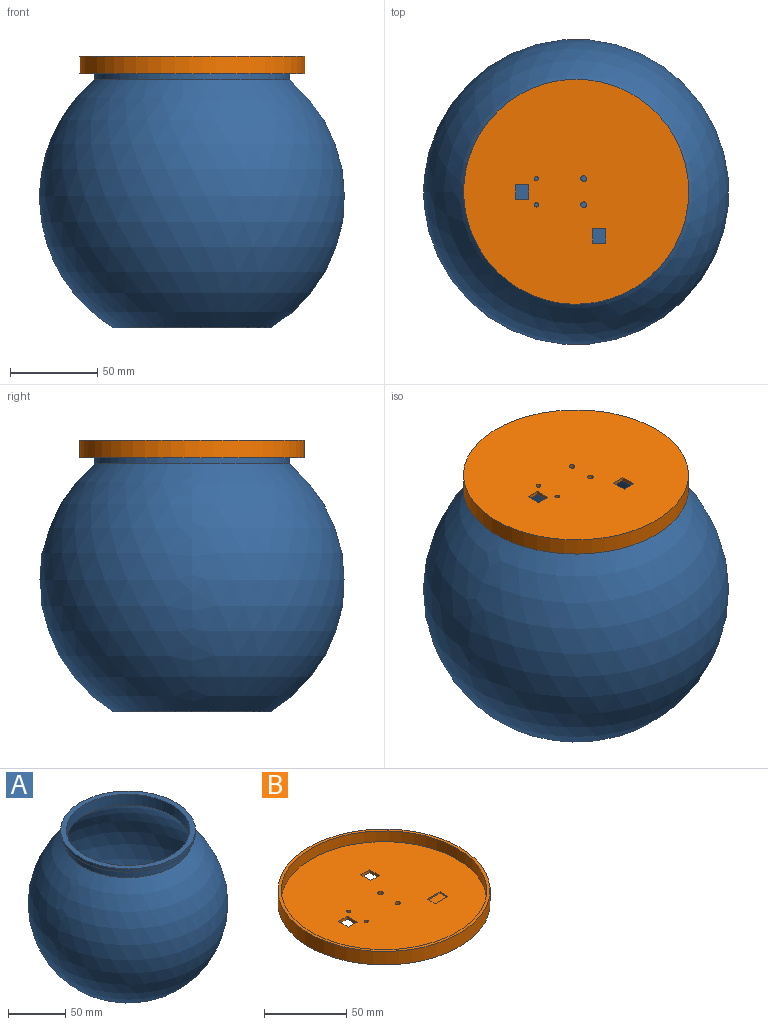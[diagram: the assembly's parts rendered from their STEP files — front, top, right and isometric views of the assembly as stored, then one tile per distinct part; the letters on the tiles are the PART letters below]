
ASSEMBLY  parts=2 mates=1
PART A: 9 faces, bbox 175x175x153.8 mm
  f0: plane 118x118mm, normal (0,0,1), area 1775mm2, adj f1,f8
  f1: cylinder r=59mm len=118mm, axis (0,0,-1), area 1297.5mm2, adj f0,f2
  f2: plane 118x118mm, normal (0,0,-1), area 1083.8mm2, adj f1,f3
  f3: cylinder r=56mm len=112mm, axis (0,0,-1), area 2814.9mm2, adj f2,f4
  f4: sphere r=87.5mm, area 78219.5mm2, adj f3,f5
  f5: plane 90x90mm, normal (0,0,-1), area 6361.7mm2, adj f4
  f6: plane 92.23x92.23mm, normal (0,0,1), area 6680.6mm2, adj f7
  f7: sphere r=86.23mm, area 75909.8mm2, adj f6,f8
  f8: cylinder r=54mm len=108mm, axis (0,0,-1), area 3901.9mm2, adj f0,f7
PART B: 22 faces, bbox 129x129x10 mm
  f0: plane 7.5x2mm, normal (0,1,0), area 15mm2, adj f1,f9,f17,f18
  f1: plane 8.5x2mm, normal (1,0,0), area 17mm2, adj f0,f2,f17,f18
  f2: plane 7.5x2mm, normal (0,-1,0), area 15mm2, adj f1,f9,f17,f18
  f3: plane 7.5x2mm, normal (0,1,0), area 15mm2, adj f4,f10,f17,f18
  f4: plane 8.5x2mm, normal (1,0,0), area 17mm2, adj f3,f5,f17,f18
  f5: plane 7.5x2mm, normal (0,-1,0), area 15mm2, adj f4,f10,f17,f18
  f6: plane 10.77x1mm, normal (0,1,0), area 10.8mm2, adj f7,f11,f17,f21
  f7: plane 6.72x1mm, normal (1,0,0), area 6.7mm2, adj f6,f8,f17,f21
  f8: plane 10.77x1mm, normal (0,-1,0), area 10.8mm2, adj f7,f11,f17,f21
  f9: plane 8.5x2mm, normal (-1,0,0), area 17mm2, adj f0,f2,f17,f18
  f10: plane 8.5x2mm, normal (-1,0,0), area 17mm2, adj f3,f5,f17,f18
  f11: plane 6.72x1mm, normal (-1,0,0), area 6.7mm2, adj f6,f8,f17,f21
  f12: cylinder r=1.25mm len=2.5mm, axis (0,0,-1), area 15.7mm2, adj f17,f18
  f13: cylinder r=1.25mm len=2.5mm, axis (0,0,-1), area 15.7mm2, adj f17,f18
  f14: cylinder r=1.65mm len=3.3mm, axis (0,0,-1), area 20.7mm2, adj f17,f18
  f15: cylinder r=1.65mm len=3.3mm, axis (0,0,-1), area 20.7mm2, adj f17,f18
  f16: cylinder r=64.5mm len=129mm, axis (0,0,-1), area 4052.7mm2, adj f18,f20
  f17: plane 125x125mm, normal (0,0,1), area 12045.1mm2, adj f0,f1,f2,f3,f4,f5,f6,f7
  f18: plane 129x129mm, normal (0,0,-1), area 12915.4mm2, adj f0,f1,f2,f3,f4,f5,f9,f10
  f19: cylinder r=62.5mm len=125mm, axis (0,0,-1), area 3141.6mm2, adj f17,f20
  f20: plane 129x129mm, normal (0,0,1), area 798mm2, adj f16,f19
  f21: plane 10.77x6.72mm, normal (0,0,1), area 72.4mm2, adj f6,f7,f8,f11
PLACE A t=(-33.25,-28.74,-8.16)mm
PLACE B rot(axis=(1,0,0),180deg) t=(-33.25,-28.74,72.58)mm
MATE cylindrical B.f19 <-> A.f1  axis (0,0,-1) through (-33.25,-28.74,62.58)mm
